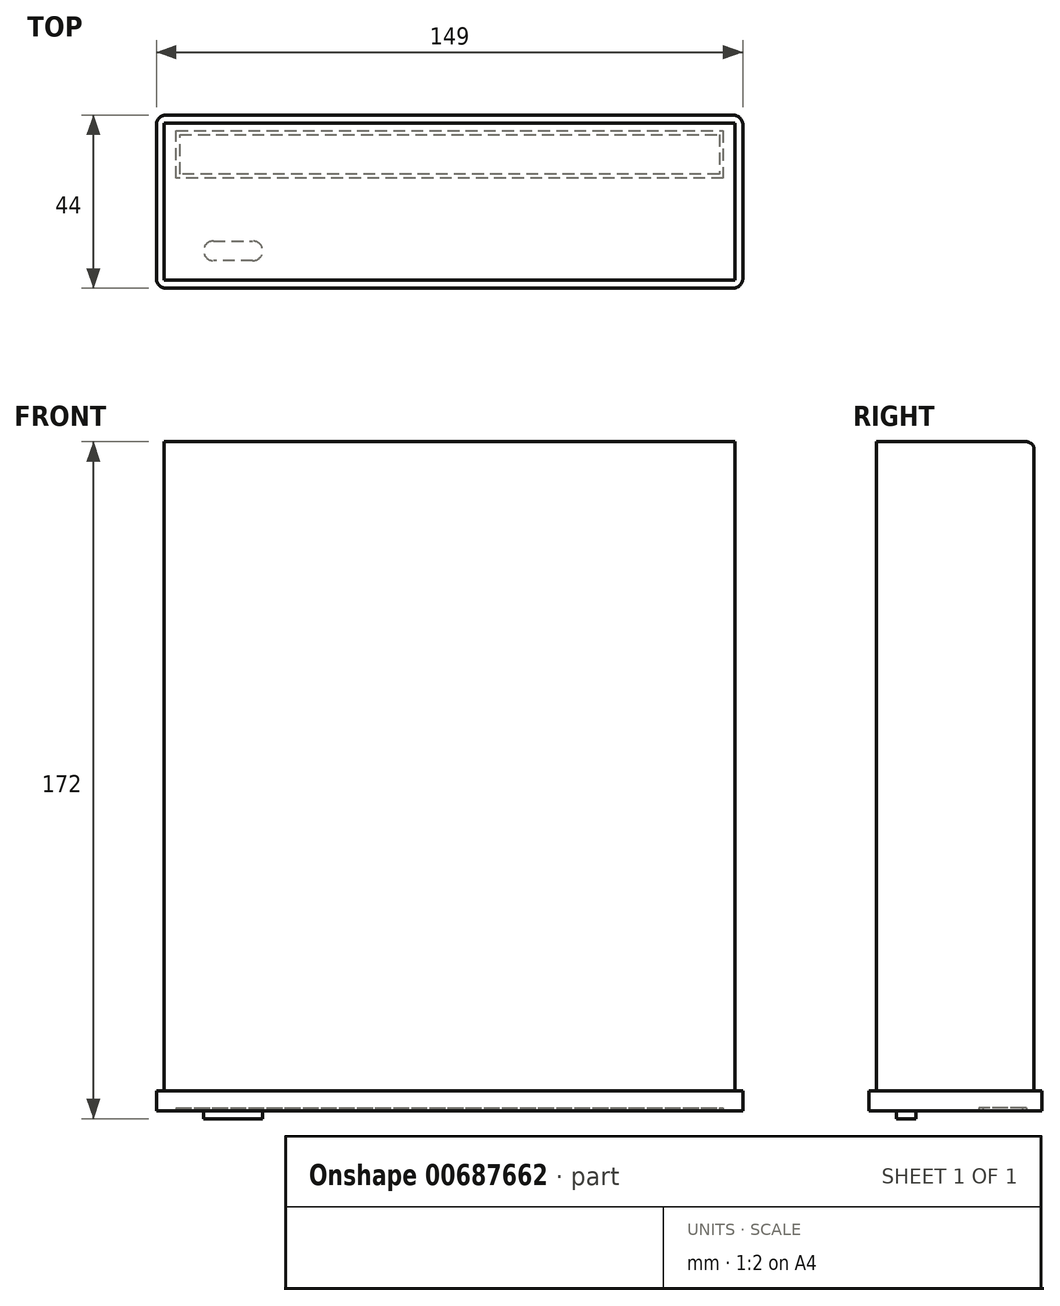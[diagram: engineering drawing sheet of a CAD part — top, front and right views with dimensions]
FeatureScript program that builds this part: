
annotation { "Feature Type Name" : "Feature", "Feature Type Description" : "" }
export const myFeature = defineFeature(function(context is Context, id is Id, definition is map)
    precondition{}
    {
        {
            var Q0;
            Q0=qCreatedBy(makeId("Top.planeOp"),FACE);
            var sketch = newSketch(context, id + "F0", { "sketchPlane" : qUnion([Q0])});
            skLineSegment(sketch, "E0", {"start": v(-51.34, 32.88) * mm, "end": v(93.66, 32.88) * mm});
            skLineSegment(sketch, "E1", {"start": v(93.66, 32.88) * mm, "end": v(93.66, -7.12) * mm});
            skLineSegment(sketch, "E2", {"start": v(93.66, -7.12) * mm, "end": v(-51.34, -7.12) * mm});
            skLineSegment(sketch, "E3", {"start": v(-51.34, -7.12) * mm, "end": v(-51.34, 32.88) * mm});
            skSolve(sketch);
        }
        {
            var Q0;
            Q0 = qSketchRegion(id + "F0", true);
            extrude(context, id + "F1", {"entities" : qUnion([Q0]), "depth" : 165 * mm, "offsetDistance" : 25 * mm});
        }
        {
            var Q0;
            Q0=makeQuery(id+"F1.opExtrude","CAP_EDGE",EDGE,{"disambiguationData":[OSD([sQuery(id+"F0.wireOp",EDGE,"E0")])],"isStart":false});
            fillet(context, id + "F2", {"entities" : qUnion([Q0]), "radius" : 2 * mm, "tangentPropagation" : true, "allowEdgeOverflow" : false});
        }
        {
            var Q0;
            Q0=makeQuery(id+"F1.opExtrude","CAP_FACE",FACE,{"disambiguationData":[OSD([sQuery(id+"F0.wireOp",EDGE,"E0"),sQuery(id+"F0.wireOp",EDGE,"E1"),sQuery(id+"F0.wireOp",EDGE,"E2"),sQuery(id+"F0.wireOp",EDGE,"E3")])],"isStart":true});
            var sketch = newSketch(context, id + "F3", { "sketchPlane" : qUnion([Q0])});
            skLineSegment(sketch, "E4", {"start": v(45.64, -32.88) * mm, "end": v(45.64, -34.88) * mm});
            skLineSegment(sketch, "E5", {"start": v(93.66, -12.88) * mm, "end": v(95.66, -12.88) * mm});
            skLineSegment(sketch, "E6", {"start": v(22.45, 7.12) * mm, "end": v(22.45, 9.12) * mm});
            skLineSegment(sketch, "E7", {"start": v(-51.34, -12.88) * mm, "end": v(-53.34, -12.88) * mm});
            skLineSegment(sketch, "E8", {"start": v(-53.34, -12.88) * mm, "end": v(-53.34, -32.38) * mm});
            skLineSegment(sketch, "E9", {"start": v(-50.84, -34.88) * mm, "end": v(45.64, -34.88) * mm});
            skLineSegment(sketch, "E10", {"start": v(45.64, -34.88) * mm, "end": v(93.16, -34.88) * mm});
            skLineSegment(sketch, "E11", {"start": v(95.66, -32.38) * mm, "end": v(95.66, 6.62) * mm});
            skLineSegment(sketch, "E12", {"start": v(93.16, 9.12) * mm, "end": v(-50.84, 9.12) * mm});
            skLineSegment(sketch, "E13", {"start": v(-53.34, 6.62) * mm, "end": v(-53.34, -12.88) * mm});
            skPoint(sketch, "E14.visualSharp", {"position": v(95.66, -34.88) * mm});
            skArc(sketch, "E14.filletArc", {"start": v(93.16, -34.88) * mm, "mid": v(94.93, -34.14) * mm, "end": v(95.66, -32.38) * mm});
            skPoint(sketch, "E15.visualSharp", {"position": v(95.66, 9.12) * mm});
            skArc(sketch, "E15.filletArc", {"start": v(95.66, 6.62) * mm, "mid": v(94.93, 8.4) * mm, "end": v(93.16, 9.12) * mm});
            skPoint(sketch, "E16.visualSharp", {"position": v(-53.34, 9.12) * mm});
            skArc(sketch, "E16.filletArc", {"start": v(-50.84, 9.12) * mm, "mid": v(-52.6, 8.4) * mm, "end": v(-53.34, 6.62) * mm});
            skPoint(sketch, "E17.visualSharp", {"position": v(-53.34, -34.88) * mm});
            skArc(sketch, "E17.filletArc", {"start": v(-53.34, -32.38) * mm, "mid": v(-52.6, -34.14) * mm, "end": v(-50.84, -34.88) * mm});
            skSolve(sketch);
        }
        {
            var Q0;
            Q0 = qSketchRegion(id + "F3", true);
            extrude(context, id + "F4", {"entities" : qUnion([Q0]), "operationType" : NewBodyOperationType.ADD, "depth" : 5 * mm, "offsetDistance" : 25 * mm});
        }
        {
            var Q0;
            Q0=makeQuery(id+"F4.opExtrude","CAP_FACE",FACE,{"disambiguationData":[OSD([sQuery(id+"F3.wireOp",EDGE,"E8"),sQuery(id+"F3.wireOp",EDGE,"E9"),sQuery(id+"F3.wireOp",EDGE,"E10"),sQuery(id+"F3.wireOp",EDGE,"E11"),sQuery(id+"F3.wireOp",EDGE,"E12"),sQuery(id+"F3.wireOp",EDGE,"E13"),sQuery(id+"F3.wireOp",EDGE,"E14.filletArc"),sQuery(id+"F3.wireOp",EDGE,"E15.filletArc"),sQuery(id+"F3.wireOp",EDGE,"E16.filletArc"),sQuery(id+"F3.wireOp",EDGE,"E17.filletArc")])],"isStart":false});
            var sketch = newSketch(context, id + "F5", { "sketchPlane" : qUnion([Q0])});
            skLineSegment(sketch, "E18", {"start": v(95.66, -27.46) * mm, "end": v(90.66, -27.46) * mm});
            skLineSegment(sketch, "E19", {"start": v(-48.34, -20.88) * mm, "end": v(-53.34, -20.88) * mm});
            skPoint(sketch, "E20.end.orphan", {"position": v(-41.34, -32.88) * mm});
            skPoint(sketch, "E20.start.orphan", {"position": v(-48.34, -32.88) * mm});
            skLineSegment(sketch, "E21", {"start": v(29.91, -34.88) * mm, "end": v(29.91, -30.88) * mm});
            skLineSegment(sketch, "E22", {"start": v(29.91, -30.88) * mm, "end": v(90.66, -30.88) * mm});
            skLineSegment(sketch, "E23", {"start": v(90.66, -30.88) * mm, "end": v(90.66, -18.88) * mm});
            skLineSegment(sketch, "E24", {"start": v(90.66, -18.88) * mm, "end": v(-48.34, -18.88) * mm});
            skLineSegment(sketch, "E25", {"start": v(-48.34, -18.88) * mm, "end": v(-48.34, -30.88) * mm});
            skLineSegment(sketch, "E26", {"start": v(-48.34, -30.88) * mm, "end": v(29.91, -30.88) * mm});
            skLineSegment(sketch, "E27", {"start": v(41.84, -30.88) * mm, "end": v(41.84, -29.88) * mm});
            skLineSegment(sketch, "E28", {"start": v(90.66, -24.88) * mm, "end": v(89.66, -24.88) * mm});
            skLineSegment(sketch, "E29", {"start": v(-48.34, -24.88) * mm, "end": v(-47.34, -24.88) * mm});
            skLineSegment(sketch, "E30", {"start": v(26.03, -18.88) * mm, "end": v(26.03, -19.88) * mm});
            skLineSegment(sketch, "E31", {"start": v(26.03, -19.88) * mm, "end": v(-47.34, -19.88) * mm});
            skLineSegment(sketch, "E32", {"start": v(-47.34, -19.88) * mm, "end": v(-47.34, -29.88) * mm});
            skLineSegment(sketch, "E33", {"start": v(-47.34, -29.88) * mm, "end": v(89.66, -29.88) * mm});
            skLineSegment(sketch, "E34", {"start": v(89.66, -29.88) * mm, "end": v(89.66, -19.88) * mm});
            skLineSegment(sketch, "E35", {"start": v(89.66, -19.88) * mm, "end": v(26.03, -19.88) * mm});
            skSolve(sketch);
        }
        {
            var Q0;
            Q0 = qSketchRegion(id + "F5", true);
            extrude(context, id + "F6", {"entities" : qUnion([Q0]), "operationType" : NewBodyOperationType.ADD, "depth" : 0.2 * mm, "offsetDistance" : 25 * mm});
        }
        {
            var Q0;
            Q0=makeQuery(id+"F6.opExtrude","CAP_FACE",FACE,{"disambiguationData":[OSD([sQuery(id+"F5.wireOp",EDGE,"E22"),sQuery(id+"F5.wireOp",EDGE,"E23"),sQuery(id+"F5.wireOp",EDGE,"E24"),sQuery(id+"F5.wireOp",EDGE,"E25"),sQuery(id+"F5.wireOp",EDGE,"E26"),sQuery(id+"F5.wireOp",EDGE,"E31"),sQuery(id+"F5.wireOp",EDGE,"E32"),sQuery(id+"F5.wireOp",EDGE,"E33"),sQuery(id+"F5.wireOp",EDGE,"E34"),sQuery(id+"F5.wireOp",EDGE,"E35")])],"isStart":false});
            extrude(context, id + "F7", {"entities" : qUnion([Q0]), "operationType" : NewBodyOperationType.REMOVE, "oppositeDirection" : true, "depth" : 1 * mm, "offsetDistance" : 25 * mm});
        }
        {
            var Q0;
            {var subQ0=sQuery(id+"F3.wireOp",EDGE,"E17.filletArc");var subQ1=sQuery(id+"F3.wireOp",EDGE,"E16.filletArc");var subQ2=sQuery(id+"F3.wireOp",EDGE,"E15.filletArc");var subQ3=sQuery(id+"F3.wireOp",EDGE,"E14.filletArc");var subQ4=sQuery(id+"F3.wireOp",EDGE,"E13");var subQ5=sQuery(id+"F3.wireOp",EDGE,"E8");var subQ6=sQuery(id+"F3.wireOp",EDGE,"E10");var subQ7=sQuery(id+"F3.wireOp",EDGE,"E9");var subQ8=sQuery(id+"F3.wireOp",EDGE,"E11");var subQ9=sQuery(id+"F3.wireOp",EDGE,"E12");Q0=makeQuery(id+"F6.boolean.opBoolean","SPLIT",FACE,{"disambiguationData":[TD([makeQuery(id+"F4.opExtrude","SWEPT_FACE",FACE,{"disambiguationData":[OSD([subQ8])]})])],"derivedFrom":makeQuery(id+"F4.opExtrude","CAP_FACE",FACE,{"disambiguationData":[OSD([subQ5,subQ7,subQ6,subQ8,subQ9,subQ4,subQ3,subQ2,subQ1,subQ0])],"isStart":false})});}
            var sketch = newSketch(context, id + "F8", { "sketchPlane" : qUnion([Q0])});
            skPoint(sketch, "E36.end.orphan", {"position": v(-36.33, 2.12) * mm});
            skLineSegment(sketch, "E37", {"start": v(-41.34, -0.38) * mm, "end": v(-41.34, -0.38) * mm});
            skLineSegment(sketch, "E38", {"start": v(-38.84, -2.88) * mm, "end": v(-28.84, -2.88) * mm});
            skLineSegment(sketch, "E39", {"start": v(-26.34, -2.88) * mm, "end": v(-26.34, 2.12) * mm});
            skLineSegment(sketch, "E40", {"start": v(-26.34, -0.38) * mm, "end": v(-26.34, -0.38) * mm});
            skPoint(sketch, "E41.start.orphan", {"position": v(-53.34, 2.12) * mm});
            skLineSegment(sketch, "E42", {"start": v(-28.84, 2.12) * mm, "end": v(-38.84, 2.12) * mm});
            skPoint(sketch, "E43.visualSharp", {"position": v(-26.34, -2.88) * mm});
            skArc(sketch, "E43.filletArc", {"start": v(-28.84, -2.88) * mm, "mid": v(-27.07, -2.14) * mm, "end": v(-26.34, -0.38) * mm});
            skPoint(sketch, "E44.visualSharp", {"position": v(-26.34, 2.12) * mm});
            skArc(sketch, "E44.filletArc", {"start": v(-26.34, -0.38) * mm, "mid": v(-27.07, 1.4) * mm, "end": v(-28.84, 2.12) * mm});
            skPoint(sketch, "E45.visualSharp", {"position": v(-41.34, -2.88) * mm});
            skArc(sketch, "E45.filletArc", {"start": v(-41.34, -0.38) * mm, "mid": v(-40.6, -2.14) * mm, "end": v(-38.84, -2.88) * mm});
            skPoint(sketch, "E46.visualSharp", {"position": v(-41.34, 2.12) * mm});
            skArc(sketch, "E46.filletArc", {"start": v(-38.84, 2.12) * mm, "mid": v(-40.6, 1.4) * mm, "end": v(-41.34, -0.38) * mm});
            skSolve(sketch);
        }
        {
            var Q0;
            Q0 = qSketchRegion(id + "F8", true);
            extrude(context, id + "F9", {"entities" : qUnion([Q0]), "operationType" : NewBodyOperationType.ADD, "depth" : 2 * mm, "offsetDistance" : 25 * mm});
        }
    });
